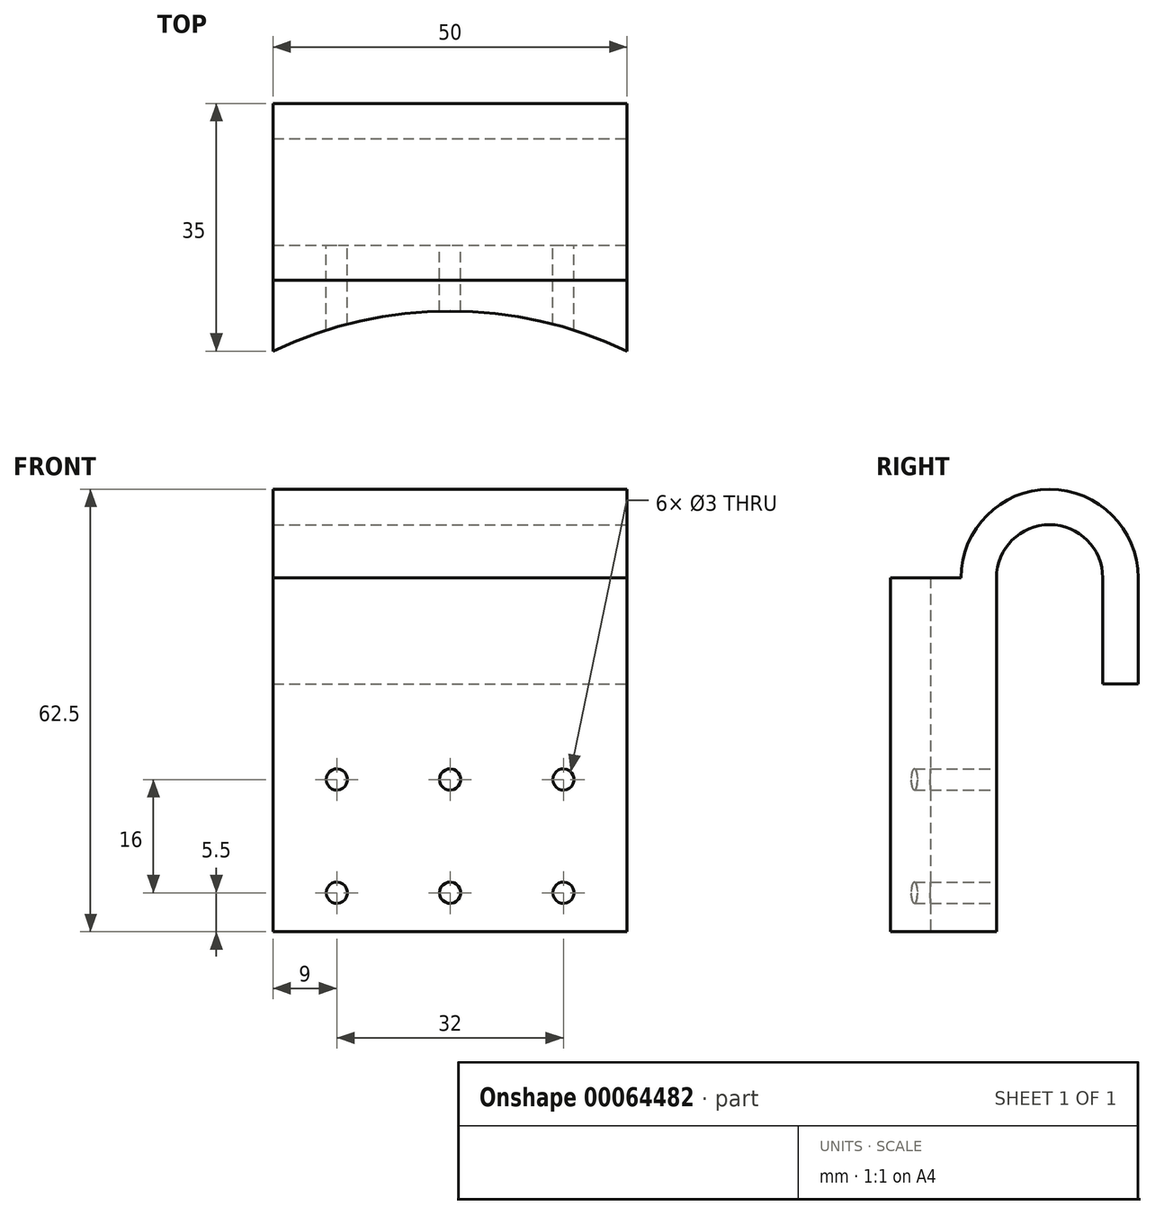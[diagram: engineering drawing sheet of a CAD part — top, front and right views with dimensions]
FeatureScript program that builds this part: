
annotation { "Feature Type Name" : "Feature", "Feature Type Description" : "" }
export const myFeature = defineFeature(function(context is Context, id is Id, definition is map)
    precondition{}
    {
        {
            var Q0;
            Q0=qCreatedBy(makeId("Top.planeOp"),FACE);
            var sketch = newSketch(context, id + "F0", { "sketchPlane" : qUnion([Q0])});
            skCircle(sketch, "E0", {"center": v(0, -58) * mm, "radius": 58 * mm});
            skLineSegment(sketch, "E1", {"start": v(25, 9.34) * mm, "end": v(25, -5.66) * mm});
            skLineSegment(sketch, "E2", {"start": v(0, -58) * mm, "end": v(0, 42.04) * mm, "construction": true});
            skLineSegment(sketch, "E3.MirrorCS", {"start": v(-25, 9.34) * mm, "end": v(-25, -5.66) * mm});
            skLineSegment(sketch, "E4", {"start": v(-25, 9.34) * mm, "end": v(25, 9.34) * mm});
            skSolve(sketch);
        }
        {
            var Q0;
            {var subQ0=sQuery(id+"F0.wireOp",EDGE,"E1");Q0=makeQuery(id+"F0.imprint","IMPRINT",FACE,{"disambiguationData":[TD([[makeQuery(id+"F0.imprint","IMPRINT",EDGE,{"derivedFrom":subQ0}),-1.0]])]});}
            extrude(context, id + "F1", {"entities" : qUnion([Q0]), "depth" : 50 * mm});
        }
        {
            var Q0;
            Q0=makeQuery(id+"F1.opExtrude","SWEPT_FACE",FACE,{"disambiguationData":[OSD([sQuery(id+"F0.wireOp",EDGE,"E1")])]});
            var sketch = newSketch(context, id + "F2", { "sketchPlane" : qUnion([Q0])});
            skLineSegment(sketch, "E5", {"start": v(24.34, 50) * mm, "end": v(24.34, 35) * mm});
            skArc(sketch, "E6", {"start": v(24.34, 50) * mm, "mid": v(16.84, 57.5) * mm, "end": v(9.34, 50) * mm});
            skArc(sketch, "E7.0", {"start": v(29.34, 50) * mm, "mid": v(16.84, 62.5) * mm, "end": v(4.34, 50) * mm});
            skLineSegment(sketch, "E7.1", {"start": v(29.34, 50) * mm, "end": v(29.34, 35) * mm});
            skLineSegment(sketch, "E8", {"start": v(24.34, 35) * mm, "end": v(29.34, 35) * mm});
            skSolve(sketch);
        }
        {
            var Q0;
            Q0=makeQuery(id+"F2.imprint","IMPRINT",FACE,{"disambiguationData":[TD([[makeQuery(id+"F2.imprint","IMPRINT",EDGE,{"derivedFrom":sQuery(id+"F2.wireOp",EDGE,"E5")}),1.0]])]});
            var Q1;
            Q1=makeQuery(id+"F1.opExtrude","SWEPT_FACE",FACE,{"disambiguationData":[OSD([sQuery(id+"F0.wireOp",EDGE,"E3.MirrorCS")])]});
            extrude(context, id + "F3", {"entities" : qUnion([Q0]), "operationType" : NewBodyOperationType.ADD, "endBound" : BoundingType.UP_TO_SURFACE, "oppositeDirection" : true, "endBoundEntityFace" : qUnion([Q1]), "depth" : 25 * mm});
        }
        {
            var Q0;
            Q0=makeQuery(id+"F1.opExtrude","SWEPT_FACE",FACE,{"disambiguationData":[OSD([sQuery(id+"F0.wireOp",EDGE,"E4")])]});
            var sketch = newSketch(context, id + "F4", { "sketchPlane" : qUnion([Q0])});
            skCircle(sketch, "E9", {"center": v(0, 21.5) * mm, "radius": 1.5 * mm});
            skPoint(sketch, "E10", {"position": v(0, 0) * mm});
            skCircle(sketch, "E11", {"center": v(16, 21.5) * mm, "radius": 1.5 * mm});
            skCircle(sketch, "E12", {"center": v(-16, 21.5) * mm, "radius": 1.5 * mm});
            skCircle(sketch, "E13", {"center": v(-16, 5.5) * mm, "radius": 1.5 * mm});
            skCircle(sketch, "E14", {"center": v(0, 5.5) * mm, "radius": 1.5 * mm});
            skCircle(sketch, "E15", {"center": v(16, 5.5) * mm, "radius": 1.5 * mm});
            skLineSegment(sketch, "E16", {"start": v(0, 0) * mm, "end": v(0, 21.5) * mm, "construction": true});
            skSolve(sketch);
        }
        {
            var Q0;
            Q0=makeQuery(id+"F4.imprint","IMPRINT",FACE,{"disambiguationData":[TD([[makeQuery(id+"F4.imprint","IMPRINT",EDGE,{"derivedFrom":sQuery(id+"F4.wireOp",EDGE,"E12")}),1.0]])]});
            var Q1;
            Q1=makeQuery(id+"F4.imprint","IMPRINT",FACE,{"disambiguationData":[TD([[makeQuery(id+"F4.imprint","IMPRINT",EDGE,{"derivedFrom":sQuery(id+"F4.wireOp",EDGE,"E9")}),1.0]])]});
            var Q2;
            Q2=makeQuery(id+"F4.imprint","IMPRINT",FACE,{"disambiguationData":[TD([[makeQuery(id+"F4.imprint","IMPRINT",EDGE,{"derivedFrom":sQuery(id+"F4.wireOp",EDGE,"E11")}),1.0]])]});
            var Q3;
            Q3=makeQuery(id+"F4.imprint","IMPRINT",FACE,{"disambiguationData":[TD([[makeQuery(id+"F4.imprint","IMPRINT",EDGE,{"derivedFrom":sQuery(id+"F4.wireOp",EDGE,"E15")}),1.0]])]});
            var Q4;
            Q4=makeQuery(id+"F4.imprint","IMPRINT",FACE,{"disambiguationData":[TD([[makeQuery(id+"F4.imprint","IMPRINT",EDGE,{"derivedFrom":sQuery(id+"F4.wireOp",EDGE,"E14")}),1.0]])]});
            var Q5;
            Q5=makeQuery(id+"F4.imprint","IMPRINT",FACE,{"disambiguationData":[TD([[makeQuery(id+"F4.imprint","IMPRINT",EDGE,{"derivedFrom":sQuery(id+"F4.wireOp",EDGE,"E13")}),1.0]])]});
            extrude(context, id + "F5", {"entities" : qUnion([Q0, Q1, Q2, Q3, Q4, Q5]), "operationType" : NewBodyOperationType.REMOVE, "endBound" : BoundingType.THROUGH_ALL, "oppositeDirection" : true, "depth" : 25 * mm});
        }
    });
